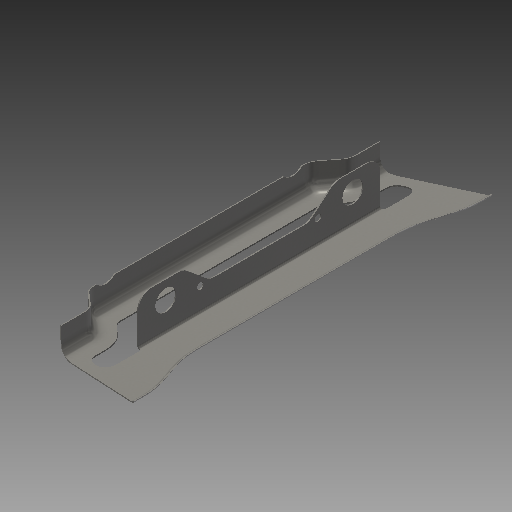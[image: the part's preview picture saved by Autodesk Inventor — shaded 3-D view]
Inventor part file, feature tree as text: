
AUTODESK INVENTOR PART (.ipt)
format: ipt  version: 2019 (Build 230136000, 136)  size: 833,536 bytes
history: native  units: mm
features: sketch x12, extrude x9, fillet x7, mirror x2, shell x1, sweep x1, hole x1, projected_geometry x1
ambient origin geometry x8: Origin, YZ Plane, XZ Plane, XY Plane, X Axis, Y Axis, Z Axis, Center Point
bodies: Solid1 (feature_tree)
feature tree (34):
  extrude  "Extrusion1"  Depth=24.799978mm
  extrude  "Extrusion2"  Depth=326.0mm TaperAngle=0.0deg
  mirror  "Mirror1"
  fillet  "Fillet1"  Radius=19.437213mm
  extrude  "Extrusion3"  Depth=100.910844mm
  fillet  "Fillet2"  Radius=341.0mm
  shell  "Shell1"  Thickness=13.613568mm
  extrude  "Extrusion4"  Depth=12.0mm
  sweep  "Sweep2"
  mirror  "Mirror3"
  extrude  "Extrusion7"  Depth=142.0mm
  extrude  "Extrusion8"  Depth=1.0mm
  fillet  "Fillet3"  Radius=1.0mm
  extrude  "Extrusion9"  Depth=341.0mm TaperAngle=0.0deg
  fillet  "Fillet4"  Radius=17.397816mm
  fillet  "Fillet5"  Radius=40.517008mm
  fillet  "Fillet6"  Radius=109.385406mm
  extrude  "Extrusion10"  TaperAngle=0.0deg  [1 undecoded]
  fillet  "Fillet7"  Radius=23.0mm
  extrude  "Extrusion11"  Depth=33.196137mm
  hole  "Hole1"  [1 undecoded]
  sketch  "Sketch1"  dims[d1=14.018111mm d2=24.799978mm]
  sketch  "Sketch2"  dims[d4=102.910705mm d5=326.0mm d6=0.0mm d7=19.437213mm]
  sketch  "Sketch3"  dims[d8=118.019695mm d9=100.910844mm d10=341.0mm d11=0.0mm d12=13.613568mm]
  sketch  "Sketch4"  dims[d13=15.0mm d14=12.0mm d15=18.019352mm]
  sketch  "Sketch11"  dims[d16=15.5mm d17=205.0mm]
  sketch  "Sketch12"  dims[d18=142.0mm d19=142.0mm]
  sketch  "Sketch13"  dims[d20=341.0mm d21=0.0mm d22=90.0mm d23=5.0mm d24=1.0mm]
  sketch  "Sketch14"  dims[d26=34.0mm d27=341.0mm d28=0.0mm d34=17.397816mm d36=40.517008mm d37=109.385406mm]
  sketch  "Sketch16"  dims[d38=180.0deg d39=0.0mm d40=23.0mm]
  sketch  "Sketch17"  dims[d41=23.0mm d42=33.196137mm]
  sketch  "Sketch18"  dims[d43=170.0mm d44=85.0mm]
  sketch  "Sketch19"  dims[d45=33.196137mm d46=5.0mm d47=0.0mm d48=5.0mm d49=5.0mm d50=5.0mm d51=40.0mm d52=5.0mm d53=5.0mm d54=10.0mm d55=10.0mm d56=1.0mm d57=0.0mm d58=8.0mm d60=1.0mm d61=42.995837mm d62=220.0mm d63=0.0mm d64=2.25mm d65=3.25mm d66=2.25mm d67=20.0mm d68=6.981317mm d69=6.981317mm d70=90.0mm d71=1.0mm d72=0.0mm d73=5.0mm d74=12.0mm d75=1.0mm d76=0.0mm d77=36.18824mm d78=169.99945mm d79=84.999725mm d80=19.0mm d81=19.0mm d82=107.0mm d83=53.5mm d84=31.633282mm d85=6.0mm d86=6.0mm d87=4.0mm d88=2.0mm d89=90.0deg d90=8.0mm d91=20.594885mm d92=0.0mm]
  projected_geometry  "Project Cut Edges3"
note: 2 required parameter values undecoded (feature->parameter linkage not recoverable at this tier; creation-order binding heuristic only, values carry confidence <= 0.55)
